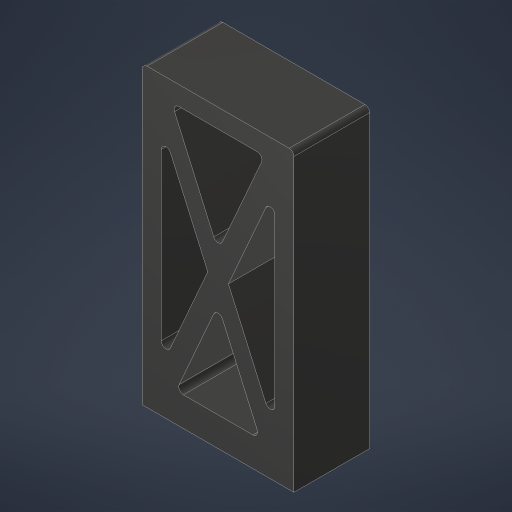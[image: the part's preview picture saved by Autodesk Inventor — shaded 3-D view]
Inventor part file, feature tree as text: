
AUTODESK INVENTOR PART (.ipt)
format: ipt  version: 2023.4 (Build 274418000, 418)  size: 229,376 bytes
history: native  units: in
note: dims shown in document units (in); Inventor stores cm internally (conversion verified against a paired STEP export)
features: sketch x3, extrude x2, projected_geometry x2, hole x1, fillet x1
ambient origin geometry x8: Origin, YZ Plane, XZ Plane, XY Plane, X Axis, Y Axis, Z Axis, Center Point
bodies: Solid1 (feature_tree)
feature tree (9):
  extrude  "Extrusion1"  Depth=1.0in
  extrude  "Extrusion2"  Depth=0.25in
  hole  "Hole1"  [1 undecoded]
  fillet  "Fillet1"  Radius=0.125in
  sketch  "Sketch1"  dims[d0=2.0in d1=1.0in]
  sketch  "Sketch2"  dims[d2=3.9in d3=0.0in d4=0.25in]
  sketch  "Sketch3"  dims[d5=0.125in d6=0.125in d7=0.125in d8=0.125in d9=0.385in d10=0.0in d11=0.0in d12=0.5in d13=0.5in d14=0.5in d15=0.2657in d16=0.75in d17=0.385in d18=0.25in d19=0.5635in d20=0.375in d21=0.0in d22=0.0625in]
  projected_geometry  "Project Cut Edges1"
  projected_geometry  "Project Cut Edges2"
note: 1 required parameter value undecoded (feature->parameter linkage not recoverable at this tier; creation-order binding heuristic only, values carry confidence <= 0.55)
